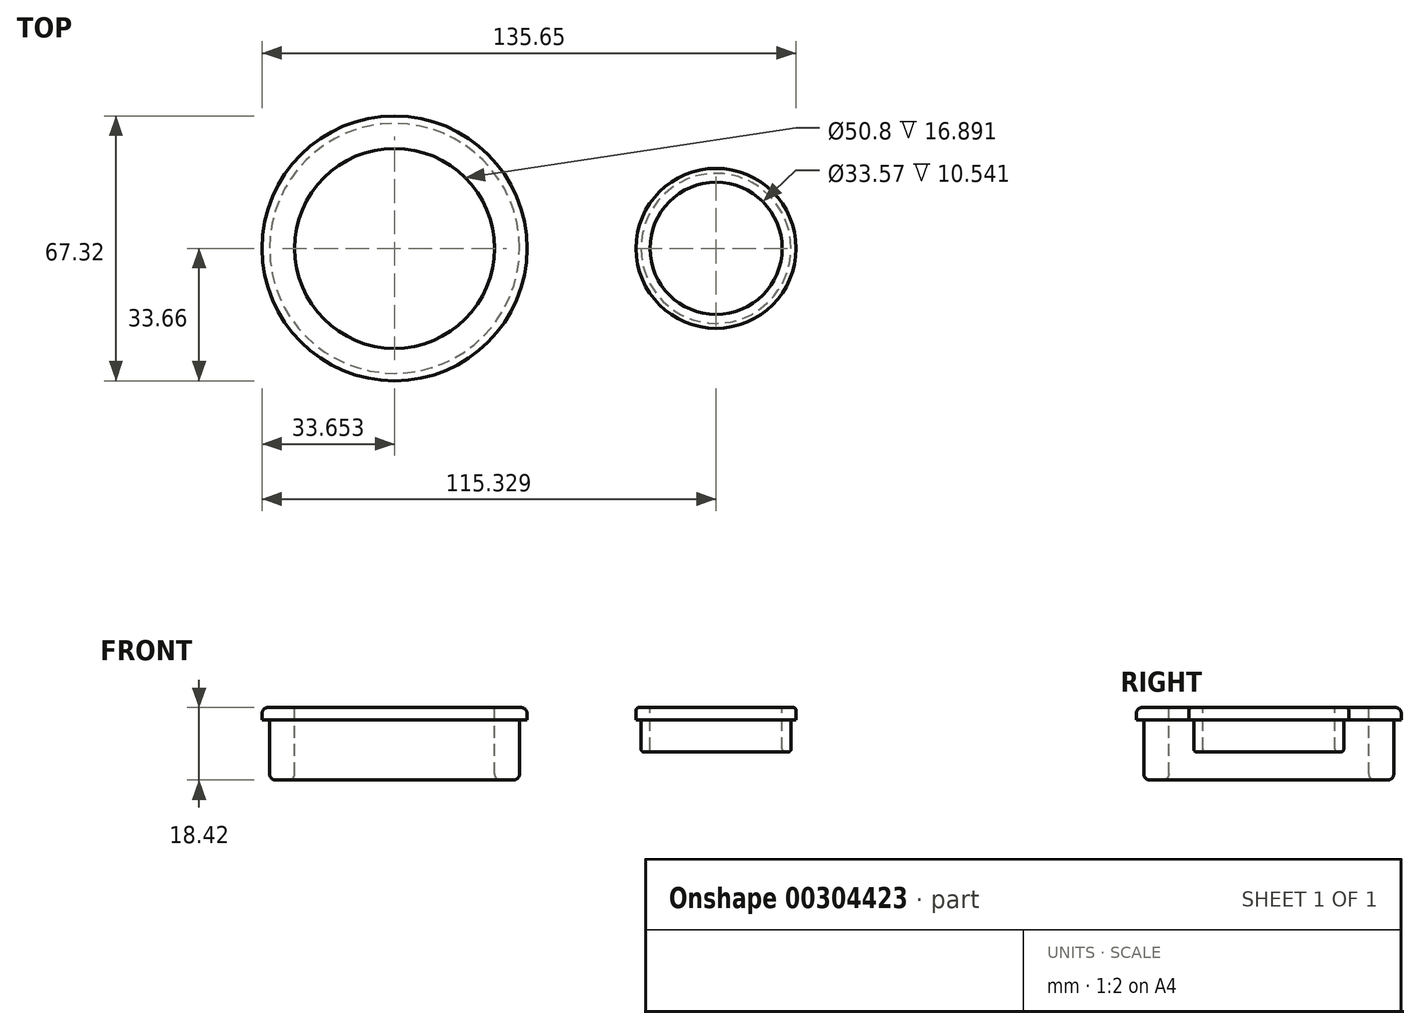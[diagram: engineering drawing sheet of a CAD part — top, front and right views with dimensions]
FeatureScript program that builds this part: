
annotation { "Feature Type Name" : "Feature", "Feature Type Description" : "" }
export const myFeature = defineFeature(function(context is Context, id is Id, definition is map)
    precondition{}
    {
        {
            var Q0;
            Q0=qCreatedBy(makeId("Top.planeOp"),FACE);
            var sketch = newSketch(context, id + "F0", { "sketchPlane" : qUnion([Q0])});
            skCircle(sketch, "E0", {"center": v(-39.15, 0) * mm, "radius": 33.66 * mm});
            skCircle(sketch, "E1", {"center": v(42.53, 0) * mm, "radius": 20.32 * mm});
            skSolve(sketch);
        }
        {
            var Q0;
            Q0 = qSketchRegion(id + "F0", true);
            extrude(context, id + "F1", {"entities" : qUnion([Q0]), "oppositeDirection" : true, "depth" : 3.17 * mm, "offsetDistance" : 25.4 * mm});
        }
        {
            var Q0;
            Q0=makeQuery(id+"F1.opExtrude","CAP_FACE",FACE,{"disambiguationData":[OSD([sQuery(id+"F0.wireOp",EDGE,"E0")])],"isStart":false});
            var sketch = newSketch(context, id + "F2", { "sketchPlane" : qUnion([Q0])});
            skCircle(sketch, "E2", {"center": v(-39.15, 0) * mm, "radius": 31.75 * mm});
            skSolve(sketch);
        }
        {
            var Q0;
            Q0 = qSketchRegion(id + "F2", true);
            extrude(context, id + "F3", {"entities" : qUnion([Q0]), "operationType" : NewBodyOperationType.ADD, "depth" : 15.24 * mm, "offsetDistance" : 25.4 * mm});
        }
        {
            var Q0;
            Q0=makeQuery(id+"F1.opExtrude","CAP_FACE",FACE,{"disambiguationData":[OSD([sQuery(id+"F0.wireOp",EDGE,"E1")])],"isStart":false});
            var sketch = newSketch(context, id + "F4", { "sketchPlane" : qUnion([Q0])});
            skCircle(sketch, "E3", {"center": v(42.53, 0) * mm, "radius": 19.05 * mm});
            skSolve(sketch);
        }
        {
            var Q0;
            Q0 = qSketchRegion(id + "F4", true);
            extrude(context, id + "F5", {"entities" : qUnion([Q0]), "operationType" : NewBodyOperationType.ADD, "depth" : 8.13 * mm, "offsetDistance" : 25.4 * mm});
        }
        {
            var Q0;
            Q0=makeQuery(id+"F1.opExtrude","CAP_FACE",FACE,{"disambiguationData":[OSD([sQuery(id+"F0.wireOp",EDGE,"E0")])],"isStart":true});
            var sketch = newSketch(context, id + "F6", { "sketchPlane" : qUnion([Q0])});
            skCircle(sketch, "E4", {"center": v(-39.15, 0) * mm, "radius": 25.4 * mm});
            skSolve(sketch);
        }
        {
            var Q0;
            Q0 = qSketchRegion(id + "F6", true);
            extrude(context, id + "F7", {"entities" : qUnion([Q0]), "operationType" : NewBodyOperationType.REMOVE, "oppositeDirection" : true, "depth" : 25.4 * mm, "offsetDistance" : 25.4 * mm});
        }
        {
            var Q0;
            Q0=makeQuery(id+"F1.opExtrude","CAP_FACE",FACE,{"disambiguationData":[OSD([sQuery(id+"F0.wireOp",EDGE,"E1")])],"isStart":true});
            var sketch = newSketch(context, id + "F8", { "sketchPlane" : qUnion([Q0])});
            skCircle(sketch, "E5", {"center": v(42.53, 0) * mm, "radius": 16.78 * mm});
            skSolve(sketch);
        }
        {
            var Q0;
            Q0 = qSketchRegion(id + "F8", true);
            extrude(context, id + "F9", {"entities" : qUnion([Q0]), "operationType" : NewBodyOperationType.REMOVE, "oppositeDirection" : true, "depth" : 25.4 * mm, "offsetDistance" : 25.4 * mm});
        }
        {
            var Q0;
            Q0=makeQuery(id+"F7.boolean.opBoolean","COPY",EDGE,{"derivedFrom":makeQuery(id+"F7.opExtrude","CAP_EDGE",EDGE,{"disambiguationData":[OSD([sQuery(id+"F6.wireOp",EDGE,"E4")])],"isStart":true})});
            var Q1;
            Q1=makeQuery(id+"F1.opExtrude","CAP_EDGE",EDGE,{"disambiguationData":[OSD([sQuery(id+"F0.wireOp",EDGE,"E0")])],"isStart":true});
            var Q2;
            Q2=makeQuery(id+"F7.boolean.opBoolean","INTERSECT",EDGE,{"derivedFrom":[makeQuery(id+"F3.opExtrude","CAP_FACE",FACE,{"disambiguationData":[OSD([sQuery(id+"F2.wireOp",EDGE,"E2")])],"isStart":false}),makeQuery(id+"F7.opExtrude","SWEPT_FACE",FACE,{"disambiguationData":[OSD([sQuery(id+"F6.wireOp",EDGE,"E4")])]})]});
            var Q3;
            Q3=makeQuery(id+"F3.opExtrude","CAP_EDGE",EDGE,{"disambiguationData":[OSD([sQuery(id+"F2.wireOp",EDGE,"E2")])],"isStart":false});
            fillet(context, id + "F10", {"entities" : qUnion([Q0, Q1, Q2, Q3]), "tangentPropagation" : true, "radius" : 1.52 * mm, "defaultsChanged" : false, "vertexSettings" : [], "allowEdgeOverflow" : false});
        }
        {
            var Q0;
            Q0=makeQuery(id+"F9.boolean.opBoolean","COPY",EDGE,{"derivedFrom":makeQuery(id+"F9.opExtrude","CAP_EDGE",EDGE,{"disambiguationData":[OSD([sQuery(id+"F8.wireOp",EDGE,"E5")])],"isStart":true})});
            var Q1;
            Q1=makeQuery(id+"F1.opExtrude","CAP_EDGE",EDGE,{"disambiguationData":[OSD([sQuery(id+"F0.wireOp",EDGE,"E1")])],"isStart":true});
            var Q2;
            Q2=makeQuery(id+"F9.boolean.opBoolean","INTERSECT",EDGE,{"derivedFrom":[makeQuery(id+"F5.opExtrude","CAP_FACE",FACE,{"disambiguationData":[OSD([sQuery(id+"F4.wireOp",EDGE,"E3")])],"isStart":false}),makeQuery(id+"F9.opExtrude","SWEPT_FACE",FACE,{"disambiguationData":[OSD([sQuery(id+"F8.wireOp",EDGE,"E5")])]})]});
            var Q3;
            Q3=makeQuery(id+"F5.opExtrude","CAP_EDGE",EDGE,{"disambiguationData":[OSD([sQuery(id+"F4.wireOp",EDGE,"E3")])],"isStart":false});
            fillet(context, id + "F11", {"entities" : qUnion([Q0, Q1, Q2, Q3]), "tangentPropagation" : true, "radius" : 0.76 * mm, "defaultsChanged" : false, "vertexSettings" : [], "allowEdgeOverflow" : false});
        }
    });
